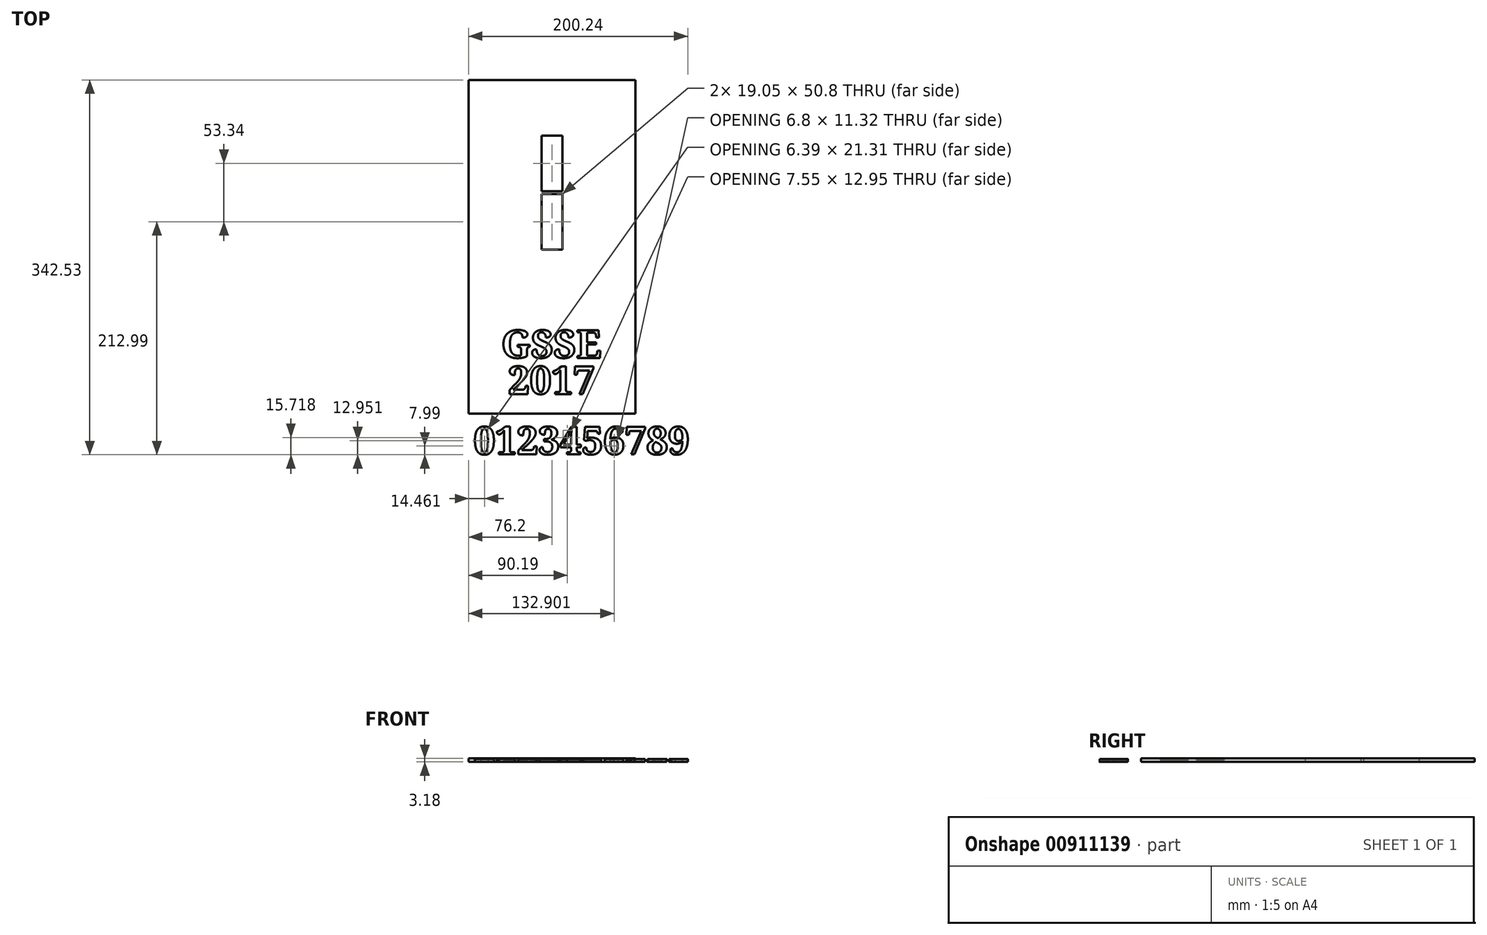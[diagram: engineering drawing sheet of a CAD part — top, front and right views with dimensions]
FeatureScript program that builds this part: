
annotation { "Feature Type Name" : "Feature", "Feature Type Description" : "" }
export const myFeature = defineFeature(function(context is Context, id is Id, definition is map)
    precondition{}
    {
        {
            var Q0;
            Q0=qCreatedBy(makeId("Top.planeOp"),FACE);
            var sketch = newSketch(context, id + "F0", { "sketchPlane" : qUnion([Q0])});
            skLineSegment(sketch, "E0.bottom", {"start": v(0, 0) * mm, "end": v(152.4, 0) * mm});
            skLineSegment(sketch, "E0.top", {"start": v(0, 304.8) * mm, "end": v(152.4, 304.8) * mm});
            skLineSegment(sketch, "E0.left", {"start": v(0, 0) * mm, "end": v(0, 304.8) * mm});
            skLineSegment(sketch, "E0.right", {"start": v(152.4, 0) * mm, "end": v(152.4, 304.8) * mm});
            skLineSegment(sketch, "E1.bottom", {"start": v(85.72, 203.2) * mm, "end": v(66.67, 203.2) * mm});
            skLineSegment(sketch, "E1.top", {"start": v(85.72, 254) * mm, "end": v(66.67, 254) * mm});
            skLineSegment(sketch, "E1.left", {"start": v(85.72, 203.2) * mm, "end": v(85.72, 254) * mm});
            skLineSegment(sketch, "E1.right", {"start": v(66.67, 203.2) * mm, "end": v(66.67, 254) * mm});
            skPoint(sketch, "E1.middle", {"position": v(76.2, 228.6) * mm});
            skLineSegment(sketch, "E2.bottom", {"start": v(85.72, 149.86) * mm, "end": v(66.67, 149.86) * mm});
            skLineSegment(sketch, "E2.top", {"start": v(85.72, 200.66) * mm, "end": v(66.67, 200.66) * mm});
            skLineSegment(sketch, "E2.left", {"start": v(85.72, 149.86) * mm, "end": v(85.72, 200.66) * mm});
            skLineSegment(sketch, "E2.right", {"start": v(66.67, 149.86) * mm, "end": v(66.67, 200.66) * mm});
            skPoint(sketch, "E2.middle", {"position": v(76.2, 175.26) * mm});
            skLineSegment(sketch, "E3", {"start": v(76.2, 304.8) * mm, "end": v(76.2, 0) * mm, "construction": true});
            skSolve(sketch);
        }
        {
            var Q0;
            Q0=makeQuery(id+"F0.imprint","IMPRINT",FACE,{"disambiguationData":[TD([[makeQuery(id+"F0.imprint","IMPRINT",EDGE,{"derivedFrom":sQuery(id+"F0.wireOp",EDGE,"E0.bottom")}),1.0]])]});
            extrude(context, id + "F1", {"entities" : qUnion([Q0]), "depth" : 3.17 * mm, "offsetDistance" : 25.4 * mm});
        }
        {
            var Q0;
            Q0=qCreatedBy(makeId("Top.planeOp"),FACE);
            var sketch = newSketch(context, id + "F2", { "sketchPlane" : qUnion([Q0])});
            skText(sketch, "E4", { "text": "0123456789", "fontName": "NotoSerif-Bold.ttf"});
            const initialGuessF2  = {"E4": [0.0046, -0.03738, 1, 0, 0.0254]};
            skSetInitialGuess(sketch, initialGuessF2);
            skSolve(sketch);
        }
        {
            var Q0;
            Q0 = qSketchRegion(id + "F2", true);
            extrude(context, id + "F3", {"entities" : qUnion([Q0]), "depth" : 2.54 * mm, "offsetDistance" : 25.4 * mm});
        }
        {
            var Q0;
            Q0=makeQuery(id+"F1.opExtrude","CAP_FACE",FACE,{"disambiguationData":[OSD([sQuery(id+"F0.wireOp",EDGE,"E0.bottom"),sQuery(id+"F0.wireOp",EDGE,"E0.top"),sQuery(id+"F0.wireOp",EDGE,"E0.left"),sQuery(id+"F0.wireOp",EDGE,"E0.right"),sQuery(id+"F0.wireOp",EDGE,"E1.bottom"),sQuery(id+"F0.wireOp",EDGE,"E1.top"),sQuery(id+"F0.wireOp",EDGE,"E1.left"),sQuery(id+"F0.wireOp",EDGE,"E1.right"),sQuery(id+"F0.wireOp",EDGE,"E2.bottom"),sQuery(id+"F0.wireOp",EDGE,"E2.top"),sQuery(id+"F0.wireOp",EDGE,"E2.left"),sQuery(id+"F0.wireOp",EDGE,"E2.right")])],"isStart":false});
            var sketch = newSketch(context, id + "F4", { "sketchPlane" : qUnion([Q0])});
            skText(sketch, "E5", { "text": "GSSE", "fontName": "NotoSerif-Bold.ttf"});
            skText(sketch, "E6", { "text": "2017", "fontName": "NotoSerif-Bold.ttf"});
            const initialGuessF4  = {"E5": [0.02986, 0.0508, 1, 0, 0.0254], "E6": [0.0362, 0.01778, 1, 0, 0.0254]};
            skSetInitialGuess(sketch, initialGuessF4);
            skSolve(sketch);
        }
        {
            var Q0;
            Q0 = qSketchRegion(id + "F4", true);
            extrude(context, id + "F5", {"entities" : qUnion([Q0]), "operationType" : NewBodyOperationType.REMOVE, "oppositeDirection" : true, "depth" : 1.27 * mm, "offsetDistance" : 25.4 * mm});
        }
    });
